# Revit family: Accessory-Flush_Actuator_Plate-KOHLER-BEVEL-K-8854T_1
name_source: partatom
category: Specialty Equipment
revit_build: Autodesk Revit 2017 (Build: 20160225_1515(x64)
units: mm (PartAtom-declared; Revit-internal decimal feet)

## family parameters
Cut with Voids When Loaded = No
Host = Face
OmniClass Number = 23.31.25.00
OmniClass Title = Toilet and Bath Specialties
Part Type = Normal
Room Calculation Point = No
Round Connector Dimension = Use Diameter
Shared = No

## types (1)
- CP-Polished Chrome
    ADA Compliant = No
    Assembly Code = C1030200
    Date Modified = 01/06/2021
    Default Elevation = 42"
    Description = Hidden water tank panel (with mechanical Hydley 100/Audian without frame)
    Finish = Kohler-Plastic-CP-Polished_Chrome
    Height = 7 5/16"
    Length = 1/2"
    Manufacturer = KOHLER Co.
    Master Format 2014 = 40 05 57.13
    Master Format 2014 Name = Manual Actuators
    Material = Plastic
    Model = K-8854T-CP
    Product Name = BEVEL
    Product Page URL = https://www.kohler.com.cn
    Type = 1
    URL = http://www.kohler.com.cn
    WaterSense Certified = No
    Width = 12 15/16"

## geometry (parser evidence)
native form markers: Sweep x5
no freeform markers — native parametric forms only
